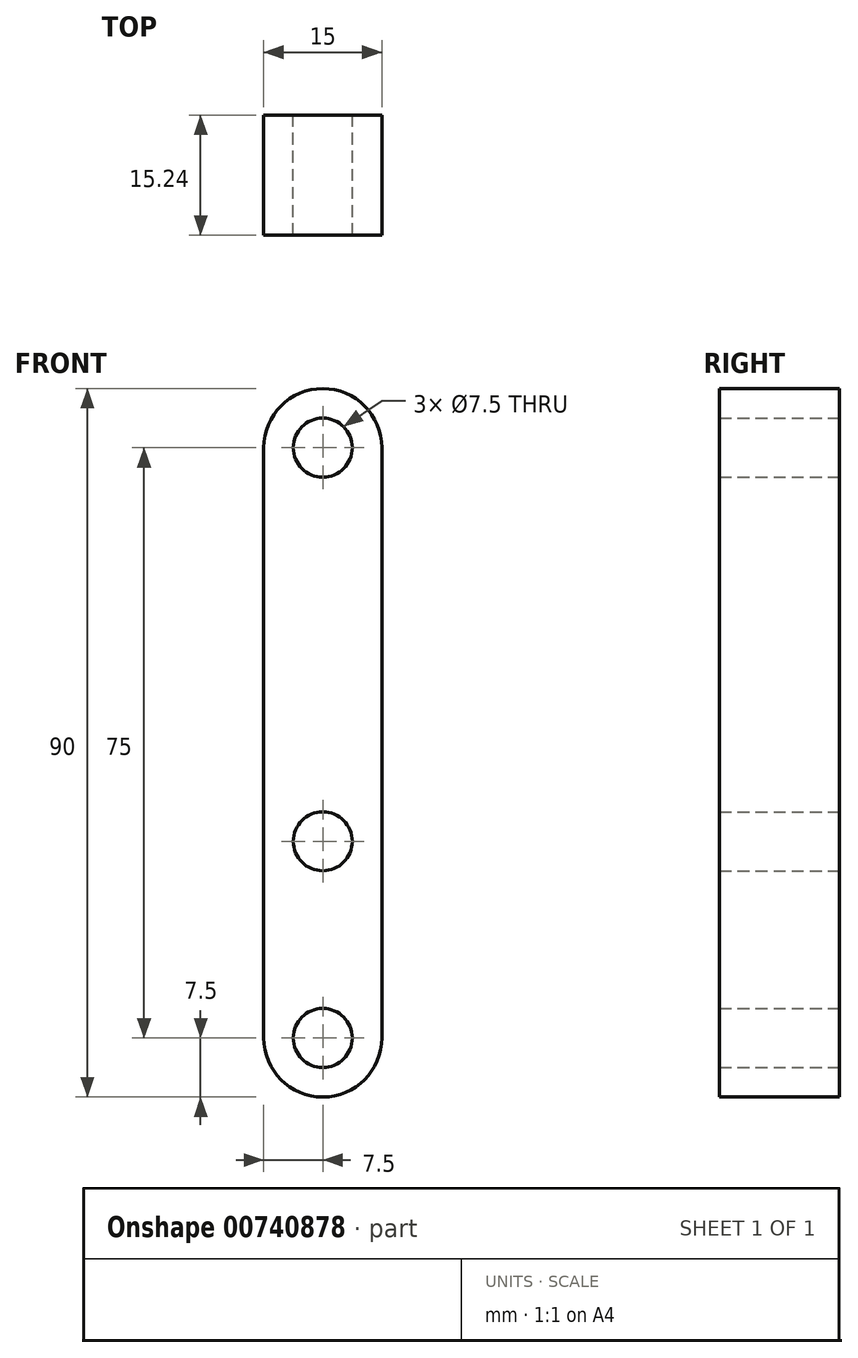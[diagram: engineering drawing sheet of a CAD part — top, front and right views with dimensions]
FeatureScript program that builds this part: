
annotation { "Feature Type Name" : "Feature", "Feature Type Description" : "" }
export const myFeature = defineFeature(function(context is Context, id is Id, definition is map)
    precondition{}
    {
        {
            var Q0;
            Q0=qCreatedBy(makeId("Front.planeOp"),FACE);
            var sketch = newSketch(context, id + "F0", { "sketchPlane" : qUnion([Q0])});
            skCircle(sketch, "E0", {"center": v(0, 0) * mm, "radius": 3.75 * mm});
            skCircle(sketch, "E1", {"center": v(0, 50) * mm, "radius": 3.75 * mm});
            skCircle(sketch, "E2", {"center": v(0, -25) * mm, "radius": 3.75 * mm});
            skCircle(sketch, "E3", {"center": v(0, 50) * mm, "radius": 7.5 * mm});
            skCircle(sketch, "E4", {"center": v(0, 0) * mm, "radius": 7.5 * mm});
            skCircle(sketch, "E5", {"center": v(0, -25) * mm, "radius": 7.5 * mm});
            skLineSegment(sketch, "E6", {"start": v(-7.5, -25) * mm, "end": v(-7.5, 50) * mm});
            skLineSegment(sketch, "E7", {"start": v(7.5, 50) * mm, "end": v(7.5, -25) * mm});
            skSolve(sketch);
        }
        {
            var Q0;
            {var subQ0=sQuery(id+"F0.wireOp",EDGE,"E6");var subQ1=sQuery(id+"F0.wireOp",EDGE,"E3");var subQ2=makeQuery(id+"F0.imprint","INTERSECT",VERTEX,{"derivedFrom":[subQ1,subQ0]});Q0=makeQuery(id+"F0.imprint","IMPRINT",FACE,{"disambiguationData":[TD([[makeQuery(id+"F0.imprint","IMPRINT",EDGE,{"disambiguationData":[TD([[subQ2,-1.0]])],"derivedFrom":subQ1}),-1.0]])]});}
            var Q1;
            Q1=makeQuery(id+"F0.imprint","IMPRINT",FACE,{"disambiguationData":[TD([[makeQuery(id+"F0.imprint","IMPRINT",EDGE,{"derivedFrom":sQuery(id+"F0.wireOp",EDGE,"E0")}),-1.0]])]});
            var Q2;
            {var subQ0=sQuery(id+"F0.wireOp",EDGE,"E6");var subQ1=sQuery(id+"F0.wireOp",EDGE,"E4");var subQ2=makeQuery(id+"F0.imprint","INTERSECT",VERTEX,{"derivedFrom":[subQ1,subQ0]});Q2=makeQuery(id+"F0.imprint","IMPRINT",FACE,{"disambiguationData":[TD([[makeQuery(id+"F0.imprint","IMPRINT",EDGE,{"disambiguationData":[TD([[subQ2,-1.0]])],"derivedFrom":subQ1}),-1.0]])]});}
            var Q3;
            Q3=makeQuery(id+"F0.imprint","IMPRINT",FACE,{"disambiguationData":[TD([[makeQuery(id+"F0.imprint","IMPRINT",EDGE,{"derivedFrom":sQuery(id+"F0.wireOp",EDGE,"E2")}),-1.0]])]});
            var Q4;
            Q4=makeQuery(id+"F0.imprint","IMPRINT",FACE,{"disambiguationData":[TD([[makeQuery(id+"F0.imprint","IMPRINT",EDGE,{"derivedFrom":sQuery(id+"F0.wireOp",EDGE,"E1")}),-1.0]])]});
            extrude(context, id + "F1", {"entities" : qUnion([Q0, Q1, Q2, Q3, Q4]), "depth" : 15.24 * mm, "offsetDistance" : 25.4 * mm});
        }
    });
